# Revit family: 306_0d6fa1bf39774ef9b193bdbab2a6dc
name_source: partatom
category: Pipe Accessories
revit_build: Autodesk Revit 2018 (Build: 20170223_1515(x64)
units: mm (PartAtom-declared; Revit-internal decimal feet)

## family parameters
Always vertical = Yes
Cut with Voids When Loaded = No
Part Type = Valve - Breaks Into
Round Connector Dimension = Use Diameter
Shared = No
Work Plane-Based = No

## types (6) — shared parameters
CAT0 = Yes
CAT1 = No
CAT2 = No
Description = Two-way valve - Flanged
L2D = 108 mm
L2D_Min = 3048 mm
Manufacturer = Azbil
P = 7 mm  [stored 0.0229659 ft]
Q = 4 mm  [stored 0.0131234 ft]
QmdConnectorList = 301;D;302;D
URL = http://acn.cn.azbil.com
W2D = 15 mm  [stored 0.0492126 ft]
magiPartTypeId = 306
magiProductFamilyId = 0d6fa1bf39774ef9b193bdbab2a6dc

## per-type parameters (varying)
- VY519XL001X: C_=23 mm  [stored 0.0754593 ft]; C_2=33 mm; D=15 mm; D1_=48 mm; G_=23 mm  [stored 0.0754593 ft]; G_2=12 mm  [stored 0.0393701 ft]; G_2__ve=-12 mm; G_4=15 mm  [stored 0.0492126 ft]; G_5=21 mm  [stored 0.0688976 ft]; H=213 mm; H1=75 mm; H1_=31 mm; H1___ve=-31 mm; H1__ve=-75 mm; H2_2=7 mm  [stored 0.0229659 ft]; H3=30 mm  [stored 0.0984252 ft]; L=108 mm; L1=50 mm; L2=66 mm; L3=28 mm  [stored 0.0918635 ft]; L_=54 mm; R=8 mm  [stored 0.0262467 ft]; T=16 mm; T_=14 mm  [stored 0.0459318 ft]; T___ve=-14 mm; W3=23 mm  [stored 0.0754593 ft]; W3_1=5 mm  [stored 0.0164042 ft]; magiProductId=7c7e011223d545d8a67da9e4a5baf7
- VY519XL002X: C_=30 mm  [stored 0.0984252 ft]; C_2=43 mm; D=25 mm; D1_=58 mm; G_=33 mm; G_2=16 mm; G_2__ve=-16 mm  [stored -0.0524934 ft]; G_4=21 mm  [stored 0.0688976 ft]; G_5=31 mm; H=228 mm; H1=90 mm; H1_=32 mm; H1___ve=-32 mm  [stored -0.104987 ft]; H1__ve=-90 mm; H2_2=7 mm  [stored 0.0229659 ft]; H3=39 mm; L=127 mm; L1=60 mm; L2=81 mm; L3=35 mm; L_=64 mm; R=13 mm  [stored 0.0426509 ft]; T=18 mm  [stored 0.0590551 ft]; T_=16 mm; T___ve=-16 mm  [stored -0.0524934 ft]; W3=28 mm  [stored 0.0918635 ft]; W3_1=6 mm  [stored 0.019685 ft]; magiProductId=01876c92037447a285ed2b030ec29a
- VY519XL004X: C_=39 mm; C_2=55 mm; D=40 mm; D1_=75 mm; G_=42 mm; G_2=21 mm  [stored 0.0688976 ft]; G_2__ve=-21 mm  [stored -0.0688976 ft]; G_4=28 mm  [stored 0.0918635 ft]; G_5=40 mm; H=241 mm; H1=103 mm; H1_=29 mm  [stored 0.0951444 ft]; H1___ve=-29 mm; H1__ve=-103 mm; H2_2=10 mm  [stored 0.0328084 ft]; H3=50 mm; L=165 mm; L1=83 mm; L2=115 mm; L3=48 mm; L_=83 mm; R=20 mm  [stored 0.0656168 ft]; T=20 mm  [stored 0.0656168 ft]; T_=18 mm  [stored 0.0590551 ft]; T___ve=-18 mm  [stored -0.0590551 ft]; W3=38 mm; W3_1=8 mm  [stored 0.0262467 ft]; magiProductId=cc8bd96c8bb34ad3bbdfd77c3e0099
- VY519XL0051: C_=44 mm; C_2=63 mm; D=50 mm; D1_=83 mm; G_=50 mm; G_2=25 mm  [stored 0.082021 ft]; G_2__ve=-25 mm  [stored -0.082021 ft]; G_4=33 mm; G_5=48 mm; H=245 mm; H1=107 mm; H1_=25 mm  [stored 0.082021 ft]; H1___ve=-25 mm  [stored -0.082021 ft]; H1__ve=-107 mm; H2_2=10 mm  [stored 0.0328084 ft]; H3=54 mm; L=178 mm; L1=89 mm; L2=128 mm; L3=51 mm; L_=89 mm; R=25 mm  [stored 0.082021 ft]; T=20 mm  [stored 0.0656168 ft]; T_=18 mm  [stored 0.0590551 ft]; T___ve=-18 mm  [stored -0.0590551 ft]; W3=43 mm; W3_1=9 mm  [stored 0.0295276 ft]; magiProductId=3693168422074a1184e9b3aecc8ab8
- VY519XL0061: C_=51 mm; C_2=73 mm; D=65 mm; D1_=93 mm; G_=59 mm; G_2=30 mm  [stored 0.0984252 ft]; G_2__ve=-30 mm  [stored -0.0984252 ft]; G_4=40 mm; G_5=57 mm; H=262 mm; H1=124 mm; H1_=33 mm; H1___ve=-33 mm  [stored -0.108268 ft]; H1__ve=-124 mm; H2_2=10 mm  [stored 0.0328084 ft]; H3=59 mm; L=190 mm; L1=90 mm; L2=136 mm; L3=55 mm; L_=95 mm; R=33 mm; T=22 mm  [stored 0.0721785 ft]; T_=20 mm  [stored 0.0656168 ft]; T___ve=-20 mm  [stored -0.0656168 ft]; W3=49 mm; W3_1=10 mm  [stored 0.0328084 ft]; magiProductId=a1907e219280489788c2c1536ea0b5
- VY519XL0081: C_=57 mm; C_2=80 mm; D=80 mm; D1_=100 mm; G_=66 mm; G_2=33 mm; G_2__ve=-33 mm  [stored -0.108268 ft]; G_4=45 mm; G_5=64 mm; H=263 mm; H1=125 mm; H1_=25 mm  [stored 0.082021 ft]; H1___ve=-25 mm  [stored -0.082021 ft]; H1__ve=-125 mm  [stored -0.410105 ft]; H2_2=10 mm  [stored 0.0328084 ft]; H3=64 mm; L=203 mm; L1=100 mm; L2=149 mm; L3=63 mm; L_=102 mm; R=40 mm; T=22 mm  [stored 0.0721785 ft]; T_=20 mm  [stored 0.0656168 ft]; T___ve=-20 mm  [stored -0.0656168 ft]; W3=55 mm; W3_1=11 mm  [stored 0.0360892 ft]; magiProductId=29451f4dc5f246c6b3ba482d496915

note: column(s) folded — value = type name in every type: MC Product Code

note: [stored X ft] marks values corroborated as IEEE doubles in the binary element streams (Revit-internal decimal feet)

## geometry (parser evidence)
native form markers: Sweep x2
no freeform markers — native parametric forms only
